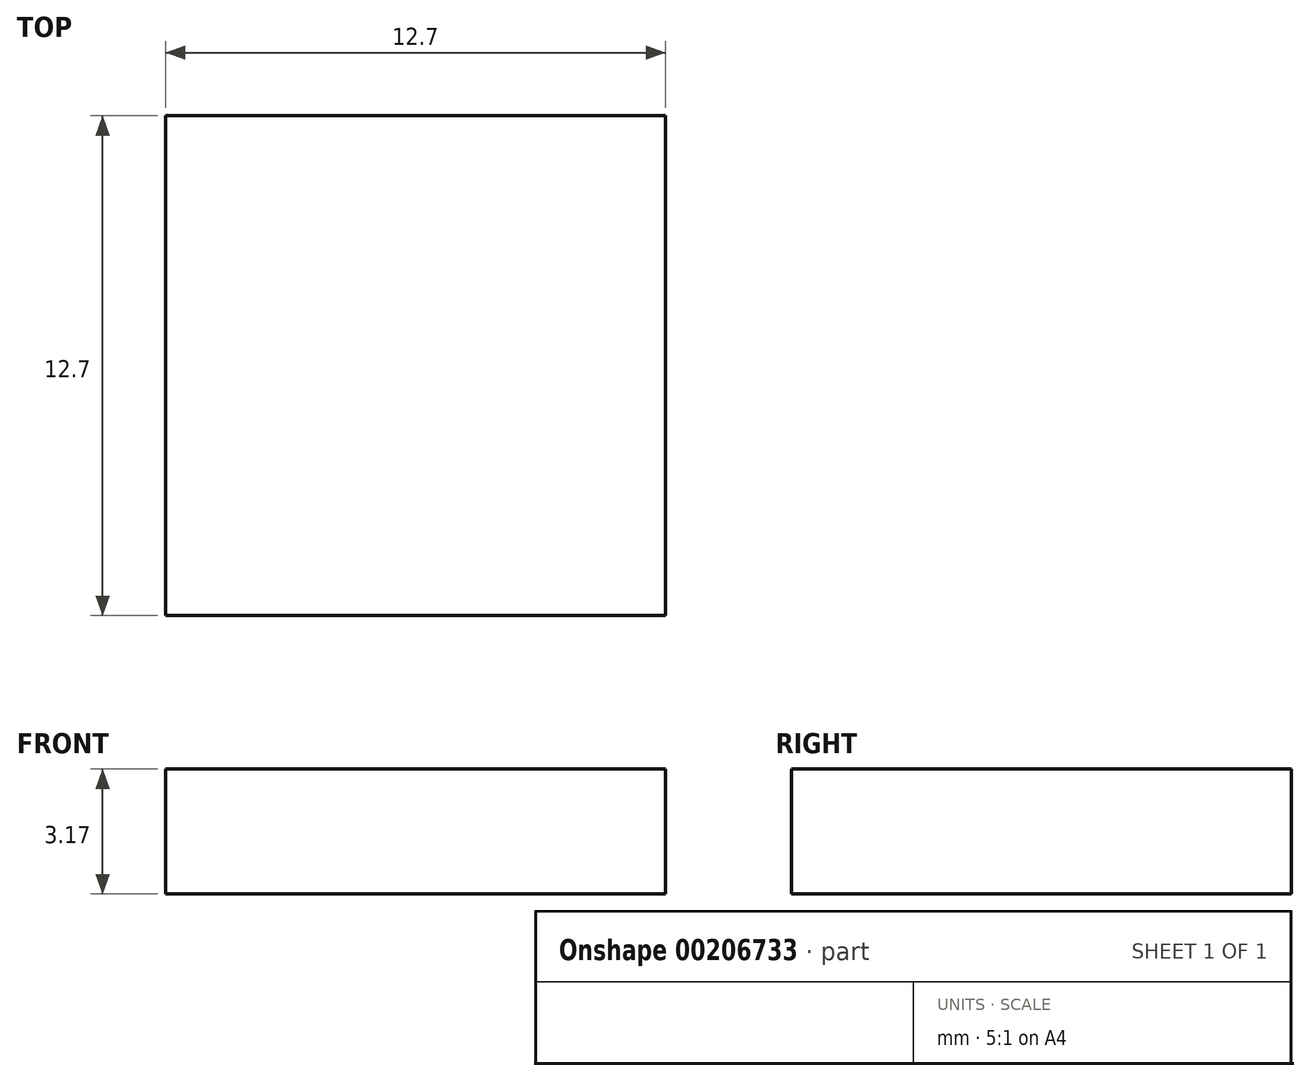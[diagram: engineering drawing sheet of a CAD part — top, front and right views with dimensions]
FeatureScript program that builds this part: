
annotation { "Feature Type Name" : "Feature", "Feature Type Description" : "" }
export const myFeature = defineFeature(function(context is Context, id is Id, definition is map)
    precondition{}
    {
        {
            var Q0;
            Q0=qCreatedBy(makeId("Top.planeOp"),FACE);
            var sketch = newSketch(context, id + "F0", { "sketchPlane" : qUnion([Q0])});
            skLineSegment(sketch, "E0.bottom", {"start": v(0, 0) * mm, "end": v(12.7, 0) * mm});
            skLineSegment(sketch, "E0.top", {"start": v(0, 12.7) * mm, "end": v(12.7, 12.7) * mm});
            skLineSegment(sketch, "E0.left", {"start": v(0, 0) * mm, "end": v(0, 12.7) * mm});
            skLineSegment(sketch, "E0.right", {"start": v(12.7, 0) * mm, "end": v(12.7, 12.7) * mm});
            skSolve(sketch);
        }
        {
            var Q0;
            Q0 = qSketchRegion(id + "F0", true);
            extrude(context, id + "F1", {"entities" : qUnion([Q0]), "depth" : 3.17 * mm});
        }
    });
